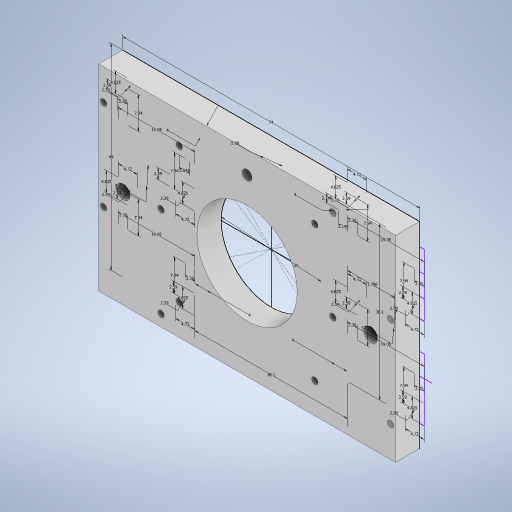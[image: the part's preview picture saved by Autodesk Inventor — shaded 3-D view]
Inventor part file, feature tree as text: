
AUTODESK INVENTOR PART (.ipt)
format: ipt  version: 2024 (Build 280153000, 153)  size: 339,968 bytes
history: native  units: in
note: dims shown in document units (in); Inventor stores cm internally (conversion verified against a paired STEP export)
features: hole x4, sketch x1, extrude x1
ambient origin geometry x8: Origin, YZ Plane, XZ Plane, XY Plane, X Axis, Y Axis, Z Axis, Center Point
bodies: Solid1 (feature_tree)
feature tree (6):
  sketch  "Sketch1"  dims[d0=2.9134in d1=1.9291in d2=0.9843in d3=1.5in d4=1.5in d5=0.0846in d6=0.0846in d7=0.464in d8=0.2362in d9=0.0in d10=0.0617in d11=0.1575in d12=0.375in d13=0.25in d14=0.5635in d15=0.1969in d16=0.0in d17=0.1339in d18=0.25in d19=0.375in d20=0.25in d21=0.5635in d22=0.328in d23=0.0in d24=0.1575in d25=0.1575in d26=0.1575in d27=0.1575in d28=0.2244in d29=0.2244in d30=0.75in d31=0.1002in d32=0.3126in d33=0.0929in d34=0.3126in d35=0.102in d36=0.102in d37=0.19in d39=0.19in d40=0.1858in d41=0.0941in d42=0.0941in d43=0.75in d44=0.0929in d45=0.3126in d46=0.0929in d47=0.3126in d48=0.102in d49=0.102in d50=0.19in d51=0.1858in d52=0.19in d53=0.1858in d54=0.0941in d55=0.0941in d56=0.75in d57=0.0929in d58=0.3126in d59=0.0929in d60=0.3126in d61=0.102in d62=0.102in d63=0.19in d64=0.1858in d65=0.19in d66=0.1858in d67=0.0941in d68=0.0941in d69=0.75in d70=0.0929in d71=0.3126in d72=0.0929in d73=0.3126in d74=0.102in d75=0.102in d76=0.19in d77=0.1858in d78=0.19in d79=0.1858in d80=0.0941in d81=0.0941in d82=0.0617in d83=0.1575in d84=0.1575in d85=0.0787in d86=90.0deg d87=0.315in d88=0.8108in d89=0.2236in d90=0.0968in d91=0.2362in d92=0.119in d93=0.0787in d94=0.5635in d95=0.315in d96=0.8108in]
  extrude  "Extrusion1"  Depth=1.9291in
  hole  "Hole1"  [1 undecoded]
  hole  "Hole2"  [1 undecoded]
  hole  "Hole3"  [1 undecoded]
  hole  "Hole4"  [1 undecoded]
note: 4 required parameter values undecoded (feature->parameter linkage not recoverable at this tier; creation-order binding heuristic only, values carry confidence <= 0.55)
